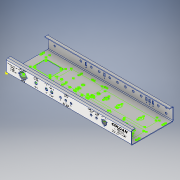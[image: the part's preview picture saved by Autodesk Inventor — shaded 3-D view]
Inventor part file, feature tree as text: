
AUTODESK INVENTOR PART (.ipt)
format: ipt  version: 2018.3 (Build 223284000, 284)  size: 2,728,960 bytes
history: native  units: in
note: dims shown in document units (in); Inventor stores cm internally (conversion verified against a paired STEP export)
features: other x16, sheet_metal_op x13, sketch x11
ambient origin geometry x8: Origin, YZ Plane, XZ Plane, XY Plane, X Axis, Y Axis, Z Axis, Center Point
bodies: Solid1 (feature_tree)
feature tree (40):
  sheet_metal_op  "Face1"
  sketch  "Sketch2"  dims[d0=23.75in]
  sheet_metal_op  "Flange1"
  sheet_metal_op  "Flange2"
  sheet_metal_op  "Flange3"
  sheet_metal_op  "Flange4"
  other  "Decal1"
  other  "Decal2"
  sketch  "Sketch11"  dims[d13=0.125in]
  sketch  "Sketch12"  dims[d14=0.125in d17=0.125in d18=0.0625in d19=0.25in d20=0.125in d21=0.75in d22=90.0deg d23=0.125in d24=0.5in d25=0.125in d26=0.125in d27=0.125in d28=0.0in d29=0.125in d30=0.0625in d31=0.25in d32=0.125in d33=2.5in d34=90.0deg d35=0.125in d36=0.5in d37=0.125in d38=0.125in d39=0.125in d40=0.0625in d41=0.25in d42=0.125in d43=0.75in d44=90.0deg d45=0.125in d46=0.5in d47=0.125in d48=0.125in d49=0.125in d50=0.0in d439=0.125in d440=0.0in]
  other  "Plate1"
  sketch  "Sketch3"  dims[d1=8.05in]
  other  "Plate2"
  sheet_metal_op  "Bend1"
  sheet_metal_op  "Corner1"
  sketch  "Sketch4"  dims[d2=0.125in]
  other  "Plate3"
  sheet_metal_op  "Bend2"
  sheet_metal_op  "Corner2"
  sketch  "Sketch5"  dims[d5=0.125in]
  sketch  "Sketch6"  dims[d6=0.0625in]
  other  "Plate4"
  sheet_metal_op  "Bend3"
  sheet_metal_op  "Corner3"
  sketch  "Sketch7"  dims[d7=0.25in]
  other  "Plate5"
  sheet_metal_op  "Bend4"
  sheet_metal_op  "Corner4"
  sketch  "Sketch8"  dims[d8=0.125in]
  sketch  "Sketch9"  dims[d9=2.5in d10=90.0deg d11=0.125in]
  sketch  "Sketch10"  dims[d12=0.5in]
  other  "Image6"
  other  "Image7"
  other  "Image8"
  other  "Image15"
  other  "Image16"
  other  "Cut2"
  other  "Cut3"
  other  "Cut4"
  other  "Definition1"
